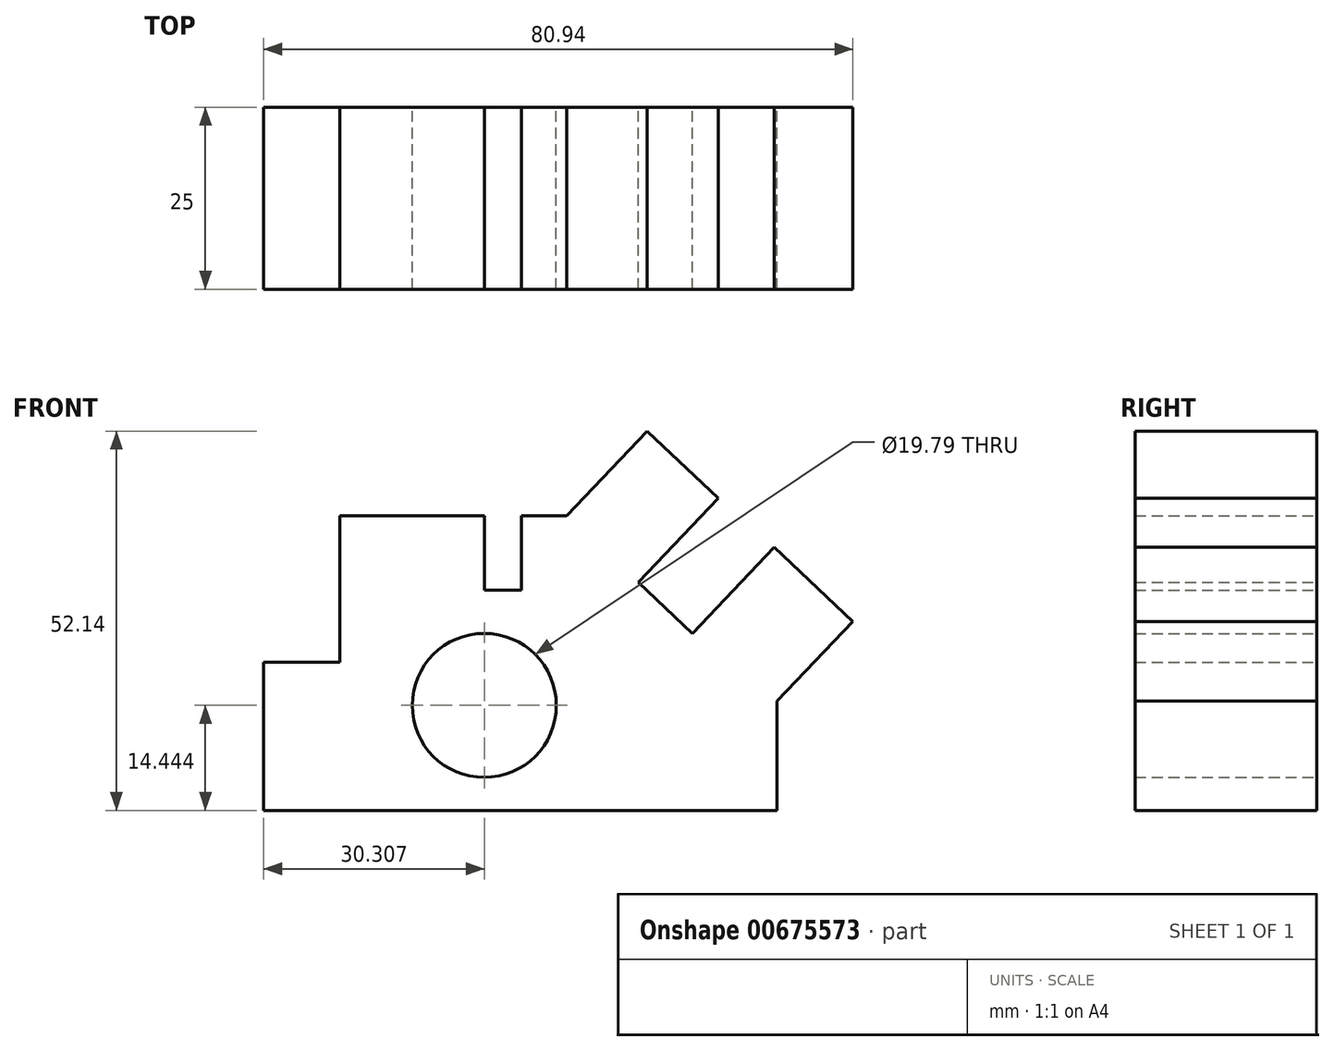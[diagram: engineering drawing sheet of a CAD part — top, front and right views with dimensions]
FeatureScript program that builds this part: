
annotation { "Feature Type Name" : "Feature", "Feature Type Description" : "" }
export const myFeature = defineFeature(function(context is Context, id is Id, definition is map)
    precondition{}
    {
        {
            var Q0;
            Q0=qCreatedBy(makeId("Front.planeOp"),FACE);
            var sketch = newSketch(context, id + "F0", { "sketchPlane" : qUnion([Q0])});
            skLineSegment(sketch, "E0", {"start": v(-40.08, -54.81) * mm, "end": v(30.45, -54.81) * mm});
            skLineSegment(sketch, "E1", {"start": v(30.45, -54.81) * mm, "end": v(30.45, -39.8) * mm});
            skLineSegment(sketch, "E2", {"start": v(-40.08, -54.81) * mm, "end": v(-40.08, -34.42) * mm});
            skLineSegment(sketch, "E3", {"start": v(-40.08, -34.42) * mm, "end": v(-29.6, -34.42) * mm});
            skLineSegment(sketch, "E4", {"start": v(-29.6, -34.42) * mm, "end": v(-29.6, -14.3) * mm});
            skLineSegment(sketch, "E5", {"start": v(-29.6, -14.3) * mm, "end": v(-9.77, -14.3) * mm});
            skLineSegment(sketch, "E6", {"start": v(-9.77, -14.3) * mm, "end": v(-9.77, -24.5) * mm});
            skLineSegment(sketch, "E7", {"start": v(-9.77, -24.5) * mm, "end": v(-4.67, -24.5) * mm});
            skLineSegment(sketch, "E8", {"start": v(-4.67, -24.5) * mm, "end": v(-4.67, -14.3) * mm});
            skCircle(sketch, "E9", {"center": v(-9.77, -40.37) * mm, "radius": 9.9 * mm});
            skLineSegment(sketch, "E10", {"start": v(40.86, -28.85) * mm, "end": v(30.45, -39.8) * mm});
            skLineSegment(sketch, "E11", {"start": v(40.86, -28.85) * mm, "end": v(30.1, -18.63) * mm});
            skLineSegment(sketch, "E12", {"start": v(30.1, -18.63) * mm, "end": v(18.84, -30.48) * mm});
            skLineSegment(sketch, "E13", {"start": v(18.84, -30.48) * mm, "end": v(11.42, -23.44) * mm});
            skLineSegment(sketch, "E14", {"start": v(11.42, -23.44) * mm, "end": v(22.36, -11.92) * mm});
            skLineSegment(sketch, "E15", {"start": v(22.36, -11.92) * mm, "end": v(12.63, -2.67) * mm});
            skLineSegment(sketch, "E16", {"start": v(12.63, -2.67) * mm, "end": v(1.57, -14.3) * mm});
            skLineSegment(sketch, "E17", {"start": v(-4.67, -14.3) * mm, "end": v(1.57, -14.3) * mm});
            skSolve(sketch);
        }
        {
            var Q0;
            Q0=makeQuery(id+"F0.imprint","IMPRINT",FACE,{"disambiguationData":[TD([[makeQuery(id+"F0.imprint","IMPRINT",EDGE,{"derivedFrom":sQuery(id+"F0.wireOp",EDGE,"E0")}),1.0]])]});
            extrude(context, id + "F1", {"entities" : qUnion([Q0]), "depth" : 25 * mm, "offsetDistance" : 25 * mm});
        }
    });
